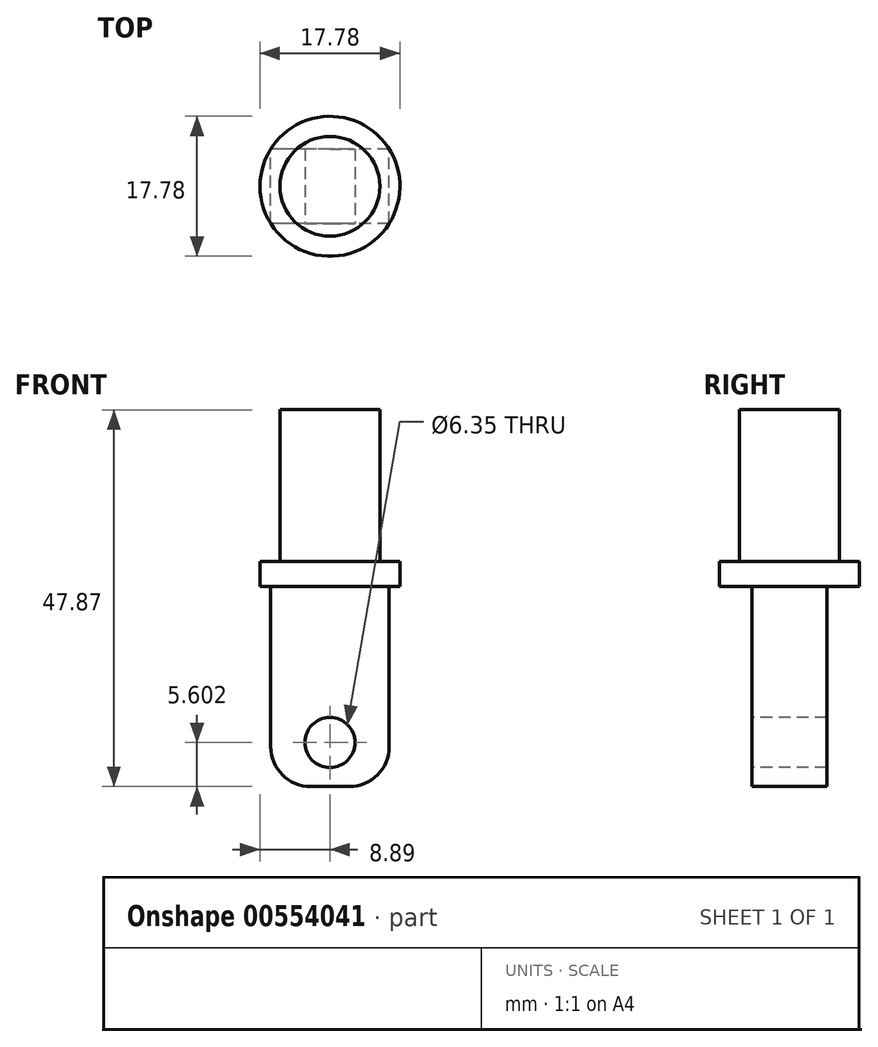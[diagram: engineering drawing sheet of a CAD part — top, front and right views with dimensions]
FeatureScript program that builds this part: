
annotation { "Feature Type Name" : "Feature", "Feature Type Description" : "" }
export const myFeature = defineFeature(function(context is Context, id is Id, definition is map)
    precondition{}
    {
        {
            var Q0;
            Q0=qCreatedBy(makeId("Top.planeOp"),FACE);
            var sketch = newSketch(context, id + "F0", { "sketchPlane" : qUnion([Q0])});
            skCircle(sketch, "E0", {"center": v(0, 0) * mm, "radius": 6.34 * mm});
            skSolve(sketch);
        }
        {
            var Q0;
            Q0 = qSketchRegion(id + "F0", true);
            extrude(context, id + "F1", {"entities" : qUnion([Q0]), "depth" : 6.6 * mm, "offsetDistance" : 25.4 * mm});
        }
        {
            var Q0;
            Q0=makeQuery(id+"F1.opExtrude","CAP_FACE",FACE,{"disambiguationData":[OSD([sQuery(id+"F0.wireOp",EDGE,"E0")])],"isStart":true});
            var sketch = newSketch(context, id + "F2", { "sketchPlane" : qUnion([Q0])});
            skCircle(sketch, "E1", {"center": v(0, 0) * mm, "radius": 8.9 * mm});
            skSolve(sketch);
        }
        {
            var Q0;
            Q0 = qSketchRegion(id + "F2", true);
            extrude(context, id + "F3", {"entities" : qUnion([Q0]), "operationType" : NewBodyOperationType.ADD, "depth" : 3.17 * mm, "offsetDistance" : 25.4 * mm});
        }
        {
            var Q0;
            Q0=makeQuery(id+"F3.opExtrude","CAP_FACE",FACE,{"disambiguationData":[OSD([sQuery(id+"F2.wireOp",EDGE,"E1")])],"isStart":false});
            var sketch = newSketch(context, id + "F4", { "sketchPlane" : qUnion([Q0])});
            skLineSegment(sketch, "E2.bottom", {"start": v(7.52, 4.74) * mm, "end": v(-7.52, 4.74) * mm});
            skLineSegment(sketch, "E2.top", {"start": v(7.52, -4.74) * mm, "end": v(-7.52, -4.74) * mm});
            skLineSegment(sketch, "E2.left", {"start": v(7.52, 4.74) * mm, "end": v(7.52, -4.74) * mm});
            skLineSegment(sketch, "E2.right", {"start": v(-7.52, 4.74) * mm, "end": v(-7.52, -4.74) * mm});
            skPoint(sketch, "E2.middle", {"position": v(0, 0) * mm});
            skSolve(sketch);
        }
        {
            var Q0;
            Q0 = qSketchRegion(id + "F4", true);
            extrude(context, id + "F5", {"entities" : qUnion([Q0]), "operationType" : NewBodyOperationType.ADD, "depth" : 25.4 * mm, "offsetDistance" : 25.4 * mm});
        }
        {
            var Q0;
            Q0=makeQuery(id+"F5.opExtrude","SWEPT_FACE",FACE,{"disambiguationData":[OSD([sQuery(id+"F4.wireOp",EDGE,"E2.bottom")])]});
            var sketch = newSketch(context, id + "F6", { "sketchPlane" : qUnion([Q0])});
            skCircle(sketch, "E3", {"center": v(0, -22.97) * mm, "radius": 3.18 * mm});
            skSolve(sketch);
        }
        {
            var Q0;
            Q0 = qSketchRegion(id + "F6", true);
            extrude(context, id + "F7", {"entities" : qUnion([Q0]), "operationType" : NewBodyOperationType.REMOVE, "oppositeDirection" : true, "depth" : 25.4 * mm, "offsetDistance" : 25.4 * mm});
        }
        {
            var Q0;
            Q0=makeQuery(id+"F5.opExtrude","CAP_EDGE",EDGE,{"disambiguationData":[OSD([sQuery(id+"F4.wireOp",EDGE,"E2.right")])],"isStart":false});
            var Q1;
            Q1=makeQuery(id+"F5.opExtrude","CAP_EDGE",EDGE,{"disambiguationData":[OSD([sQuery(id+"F4.wireOp",EDGE,"E2.left")])],"isStart":false});
            fillet(context, id + "F8", {"entities" : qUnion([Q0, Q1]), "tangentPropagation" : true, "radius" : 5.08 * mm, "defaultsChanged" : false, "vertexSettings" : [], "allowEdgeOverflow" : false});
        }
        {
            var Q0;
            Q0=makeQuery(id+"F1.opExtrude","CAP_FACE",FACE,{"disambiguationData":[OSD([sQuery(id+"F0.wireOp",EDGE,"E0")])],"isStart":false});
            extrude(context, id + "F9", {"entities" : qUnion([Q0]), "operationType" : NewBodyOperationType.ADD, "depth" : 12.7 * mm, "offsetDistance" : 25.4 * mm});
        }
    });
